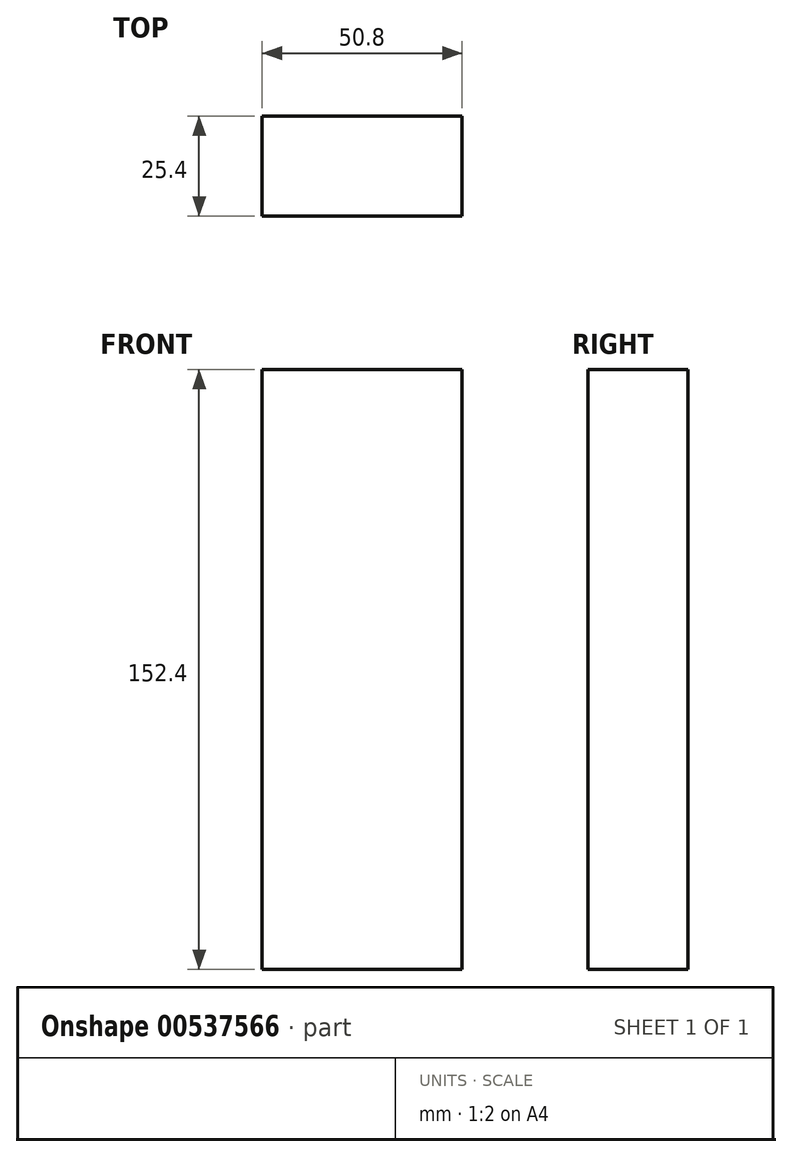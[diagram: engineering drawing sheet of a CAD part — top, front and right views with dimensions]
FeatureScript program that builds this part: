
annotation { "Feature Type Name" : "Feature", "Feature Type Description" : "" }
export const myFeature = defineFeature(function(context is Context, id is Id, definition is map)
    precondition{}
    {
        {
            var Q0;
            Q0=qCreatedBy(makeId("Top.planeOp"),FACE);
            var sketch = newSketch(context, id + "F0", { "sketchPlane" : qUnion([Q0])});
            skLineSegment(sketch, "E0.bottom", {"start": v(0, 0) * mm, "end": v(50.8, 0) * mm});
            skLineSegment(sketch, "E0.top", {"start": v(0, -25.4) * mm, "end": v(50.8, -25.4) * mm});
            skLineSegment(sketch, "E0.left", {"start": v(0, 0) * mm, "end": v(0, -25.4) * mm});
            skLineSegment(sketch, "E0.right", {"start": v(50.8, 0) * mm, "end": v(50.8, -25.4) * mm});
            skSolve(sketch);
        }
        {
            var Q0;
            Q0=makeQuery(id+"F0.imprint","IMPRINT",FACE,{"disambiguationData":[TD([[makeQuery(id+"F0.imprint","IMPRINT",EDGE,{"derivedFrom":sQuery(id+"F0.wireOp",EDGE,"E0.bottom")}),-1.0]])]});
            extrude(context, id + "F1", {"entities" : qUnion([Q0]), "depth" : 152.4 * mm, "offsetDistance" : 25.4 * mm});
        }
    });
